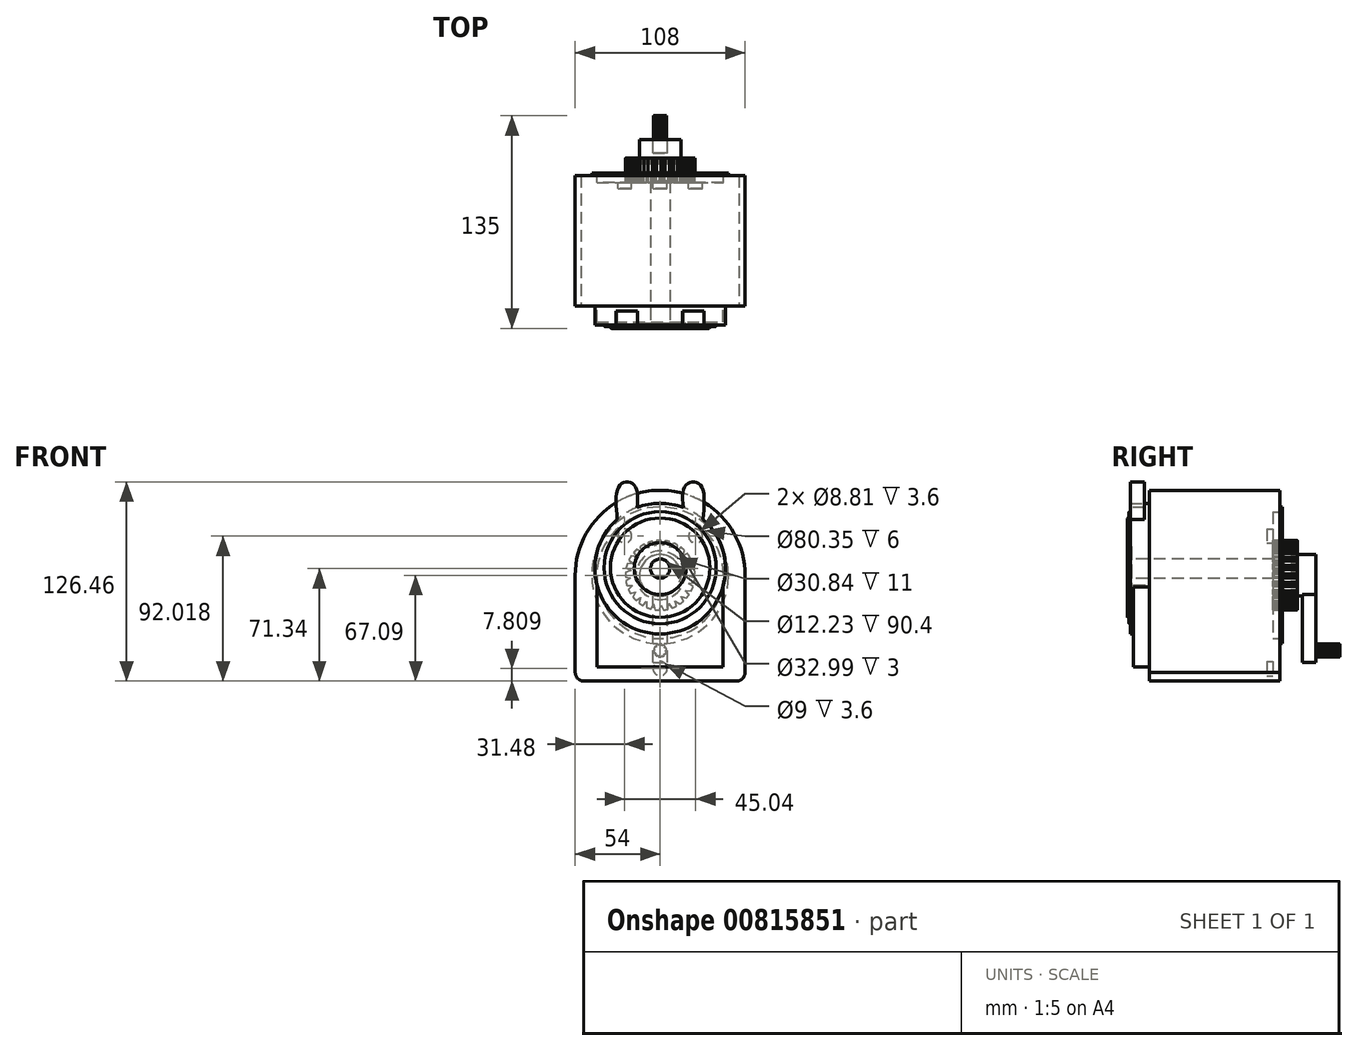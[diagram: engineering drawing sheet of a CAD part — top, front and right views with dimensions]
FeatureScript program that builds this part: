
annotation { "Feature Type Name" : "Feature", "Feature Type Description" : "" }
export const myFeature = defineFeature(function(context is Context, id is Id, definition is map)
    precondition{}
    {
        {
            var Q0;
            Q0=qCreatedBy(makeId("Front.planeOp"),FACE);
            var sketch = newSketch(context, id + "F0", { "sketchPlane" : qUnion([Q0])});
            skLineSegment(sketch, "E0.bottom", {"start": v(54, 61) * mm, "end": v(-54, 61) * mm});
            skLineSegment(sketch, "E0.top", {"start": v(54, -61) * mm, "end": v(-54, -61) * mm});
            skLineSegment(sketch, "E0.left", {"start": v(54, 61) * mm, "end": v(54, -61) * mm});
            skLineSegment(sketch, "E0.right", {"start": v(-54, 61) * mm, "end": v(-54, -61) * mm});
            skPoint(sketch, "E0.middle", {"position": v(0, 0) * mm});
            skSolve(sketch);
        }
        {
            var Q0;
            Q0=makeQuery(id+"F0.imprint","IMPRINT",FACE,{"disambiguationData":[TD([[makeQuery(id+"F0.imprint","IMPRINT",EDGE,{"derivedFrom":sQuery(id+"F0.wireOp",EDGE,"E0.bottom")}),1.0]])]});
            extrude(context, id + "F1", {"entities" : qUnion([Q0]), "depth" : 54 * mm, "offsetDistance" : 25 * mm});
        }
        {
            var Q0;
            Q0=makeQuery(id+"F1.opExtrude","CAP_FACE",FACE,{"disambiguationData":[OSD([sQuery(id+"F0.wireOp",EDGE,"E0.bottom"),sQuery(id+"F0.wireOp",EDGE,"E0.top"),sQuery(id+"F0.wireOp",EDGE,"E0.left"),sQuery(id+"F0.wireOp",EDGE,"E0.right")])],"isStart":true});
            extrude(context, id + "F2", {"entities" : qUnion([Q0]), "operationType" : NewBodyOperationType.ADD, "depth" : 29 * mm, "offsetDistance" : 25 * mm});
        }
        {
            var Q0;
            Q0=makeQuery(id+"F1.opExtrude","CAP_FACE",FACE,{"disambiguationData":[OSD([sQuery(id+"F0.wireOp",EDGE,"E0.bottom"),sQuery(id+"F0.wireOp",EDGE,"E0.top"),sQuery(id+"F0.wireOp",EDGE,"E0.left"),sQuery(id+"F0.wireOp",EDGE,"E0.right")])],"isStart":false});
            var sketch = newSketch(context, id + "F3", { "sketchPlane" : qUnion([Q0])});
            skCircle(sketch, "E1", {"center": v(0, 6.1) * mm, "radius": 54 * mm});
            skSolve(sketch);
        }
        {
            var Q0;
            {var subQ5=makeQuery(id+"F1.opExtrude","CAP_EDGE",EDGE,{"disambiguationData":[OSD([sQuery(id+"F0.wireOp",EDGE,"E0.bottom")])],"isStart":false});Q0=makeQuery(id+"F3.imprint","IMPRINT",FACE,{"disambiguationData":[TD([[makeQuery(id+"F3.imprint","IMPRINT",EDGE,{"derivedFrom":subQ5}),1.0]])]});}
            extrude(context, id + "F4", {"entities" : qUnion([Q0]), "operationType" : NewBodyOperationType.REMOVE, "oppositeDirection" : true, "depth" : 151.9 * mm, "offsetDistance" : 25 * mm});
        }
        {
            var Q0;
            Q0=makeQuery(id+"F1.opExtrude","CAP_FACE",FACE,{"disambiguationData":[OSD([sQuery(id+"F0.wireOp",EDGE,"E0.bottom"),sQuery(id+"F0.wireOp",EDGE,"E0.top"),sQuery(id+"F0.wireOp",EDGE,"E0.left"),sQuery(id+"F0.wireOp",EDGE,"E0.right")])],"isStart":false});
            var sketch = newSketch(context, id + "F5", { "sketchPlane" : qUnion([Q0])});
            skFitSpline(sketch, "E2", {"points": [v(54, -55.55) * mm, v(52.89, -58.83) * mm, v(50.2, -61) * mm], "startDerivative": vector(-1.44, -7.12) * mm, "endDerivative": vector(-6.17, -3.79) * mm});
            skFitSpline(sketch, "E3.MirrorCS", {"points": [v(-54, -55.55) * mm, v(-52.89, -58.83) * mm, v(-50.2, -61) * mm], "startDerivative": vector(1.44, -7.12) * mm, "endDerivative": vector(6.17, -3.79) * mm});
            skSolve(sketch);
        }
        {
            var Q0;
            {var subQ0=sQuery(id+"F5.wireOp",EDGE,"E3.MirrorCS");Q0=makeQuery(id+"F5.imprint","IMPRINT",FACE,{"disambiguationData":[TD([[makeQuery(id+"F5.imprint","IMPRINT",EDGE,{"derivedFrom":subQ0}),-1.0]])]});}
            extrude(context, id + "F6", {"entities" : qUnion([Q0]), "operationType" : NewBodyOperationType.REMOVE, "oppositeDirection" : true, "depth" : 499.5 * mm, "offsetDistance" : 25 * mm});
        }
        {
            var Q0;
            {var subQ0=sQuery(id+"F5.wireOp",EDGE,"E2");Q0=makeQuery(id+"F5.imprint","IMPRINT",FACE,{"disambiguationData":[TD([[makeQuery(id+"F5.imprint","IMPRINT",EDGE,{"derivedFrom":subQ0}),1.0]])]});}
            extrude(context, id + "F7", {"entities" : qUnion([Q0]), "operationType" : NewBodyOperationType.REMOVE, "oppositeDirection" : true, "depth" : 123.2 * mm, "offsetDistance" : 25 * mm});
        }
        {
            var Q0;
            Q0=makeQuery(id+"F1.opExtrude","CAP_FACE",FACE,{"disambiguationData":[OSD([sQuery(id+"F0.wireOp",EDGE,"E0.bottom"),sQuery(id+"F0.wireOp",EDGE,"E0.top"),sQuery(id+"F0.wireOp",EDGE,"E0.left"),sQuery(id+"F0.wireOp",EDGE,"E0.right")])],"isStart":false});
            var sketch = newSketch(context, id + "F8", { "sketchPlane" : qUnion([Q0])});
            skCircle(sketch, "E4", {"center": v(0, 10.34) * mm, "radius": 41.5 * mm});
            skLineSegment(sketch, "E5.bottom", {"start": v(-40.2, 0) * mm, "end": v(39.8, 0) * mm});
            skLineSegment(sketch, "E5.top", {"start": v(-40.2, -52) * mm, "end": v(39.8, -52) * mm});
            skLineSegment(sketch, "E5.left", {"start": v(-40.2, 0) * mm, "end": v(-40.2, -52) * mm});
            skLineSegment(sketch, "E5.right", {"start": v(39.8, 0) * mm, "end": v(39.8, -52) * mm});
            skSolve(sketch);
        }
        {
            var Q0;
            {var subQ0=sQuery(id+"F8.wireOp",EDGE,"E5.bottom");Q0=makeQuery(id+"F8.imprint","IMPRINT",FACE,{"disambiguationData":[TD([[makeQuery(id+"F8.imprint","IMPRINT",EDGE,{"derivedFrom":subQ0}),1.0]])]});}
            extrude(context, id + "F9", {"entities" : qUnion([Q0]), "operationType" : NewBodyOperationType.ADD, "depth" : 12 * mm, "offsetDistance" : 25 * mm});
        }
        {
            var Q0;
            {var subQ0=sQuery(id+"F8.wireOp",EDGE,"E5.bottom");Q0=makeQuery(id+"F8.imprint","IMPRINT",FACE,{"disambiguationData":[TD([[makeQuery(id+"F8.imprint","IMPRINT",EDGE,{"derivedFrom":subQ0}),-1.0]])]});}
            extrude(context, id + "F10", {"entities" : qUnion([Q0]), "operationType" : NewBodyOperationType.ADD, "depth" : 12 * mm, "offsetDistance" : 25 * mm});
        }
        {
            var Q0;
            {var subQ4=sQuery(id+"F8.wireOp",EDGE,"E5.top");Q0=makeQuery(id+"F8.imprint","IMPRINT",FACE,{"disambiguationData":[TD([[makeQuery(id+"F8.imprint","IMPRINT",EDGE,{"derivedFrom":subQ4}),1.0]])]});}
            extrude(context, id + "F11", {"entities" : qUnion([Q0]), "operationType" : NewBodyOperationType.ADD, "depth" : 10 * mm, "offsetDistance" : 25 * mm});
        }
        {
            var Q0;
            {var subQ0=sQuery(id+"F8.wireOp",EDGE,"E5.right");var subQ1=sQuery(id+"F8.wireOp",EDGE,"E5.bottom");var subQ2=sQuery(id+"F8.wireOp",EDGE,"E4");Q0=makeQuery(id+"F10.boolean.opBoolean","MERGE",FACE,{"derivedFrom":[makeQuery(id+"F9.opExtrude","CAP_FACE",FACE,{"disambiguationData":[OSD([subQ2,subQ1,subQ0])],"isStart":false}),makeQuery(id+"F10.opExtrude","CAP_FACE",FACE,{"disambiguationData":[OSD([subQ2,subQ1,subQ0])],"isStart":false})]});}
            var sketch = newSketch(context, id + "F12", { "sketchPlane" : qUnion([Q0])});
            skCircle(sketch, "E6", {"center": v(0, 10.34) * mm, "radius": 16.5 * mm});
            skCircle(sketch, "E7", {"center": v(0, 10.34) * mm, "radius": 6.12 * mm});
            skSolve(sketch);
        }
        {
            var Q0;
            Q0=makeQuery(id+"F12.imprint","IMPRINT",FACE,{"disambiguationData":[TD([[makeQuery(id+"F12.imprint","IMPRINT",EDGE,{"derivedFrom":sQuery(id+"F12.wireOp",EDGE,"E6")}),1.0]])]});
            extrude(context, id + "F13", {"entities" : qUnion([Q0]), "operationType" : NewBodyOperationType.REMOVE, "oppositeDirection" : true, "depth" : 1 * mm, "offsetDistance" : 25 * mm});
        }
        {
            var Q0;
            {var subQ0=sQuery(id+"F8.wireOp",EDGE,"E5.right");var subQ1=sQuery(id+"F8.wireOp",EDGE,"E5.bottom");var subQ2=sQuery(id+"F8.wireOp",EDGE,"E4");Q0=makeQuery(id+"F13.boolean.opBoolean","SPLIT",FACE,{"disambiguationData":[TD([makeQuery(id+"F13.opExtrude","SWEPT_FACE",FACE,{"disambiguationData":[OSD([sQuery(id+"F12.wireOp",EDGE,"E7")])]})])],"derivedFrom":makeQuery(id+"F10.boolean.opBoolean","MERGE",FACE,{"derivedFrom":[makeQuery(id+"F9.opExtrude","CAP_FACE",FACE,{"disambiguationData":[OSD([subQ2,subQ1,subQ0])],"isStart":false}),makeQuery(id+"F10.opExtrude","CAP_FACE",FACE,{"disambiguationData":[OSD([subQ2,subQ1,subQ0])],"isStart":false})]})});}
            extrude(context, id + "F14", {"entities" : qUnion([Q0]), "operationType" : NewBodyOperationType.REMOVE, "oppositeDirection" : true, "depth" : 91.4 * mm, "offsetDistance" : 25 * mm});
        }
        {
            var Q0;
            Q0=makeQuery(id+"F2.opExtrude","CAP_FACE",FACE,{"disambiguationData":[OSD([sQuery(id+"F0.wireOp",EDGE,"E0.bottom"),sQuery(id+"F0.wireOp",EDGE,"E0.top"),sQuery(id+"F0.wireOp",EDGE,"E0.left"),sQuery(id+"F0.wireOp",EDGE,"E0.right")])],"isStart":false});
            var sketch = newSketch(context, id + "F15", { "sketchPlane" : qUnion([Q0])});
            skCircle(sketch, "E8", {"center": v(0, 6.1) * mm, "radius": 22.12 * mm});
            skCircle(sketch, "E9", {"center": v(0, 6.1) * mm, "radius": 15.42 * mm});
            skCircle(sketch, "E10", {"center": v(0, 6.1) * mm, "radius": 13.17 * mm});
            skCircle(sketch, "E11", {"center": v(0, 6.1) * mm, "radius": 43.43 * mm});
            skCircle(sketch, "E12", {"center": v(0, 6.1) * mm, "radius": 40.17 * mm});
            skSolve(sketch);
        }
        {
            var Q0;
            Q0=makeQuery(id+"F15.imprint","IMPRINT",FACE,{"disambiguationData":[TD([[makeQuery(id+"F15.imprint","IMPRINT",EDGE,{"derivedFrom":sQuery(id+"F15.wireOp",EDGE,"E8")}),1.0]])]});
            extrude(context, id + "F16", {"entities" : qUnion([Q0]), "operationType" : NewBodyOperationType.ADD, "depth" : 11 * mm, "offsetDistance" : 25 * mm});
        }
        {
            var Q0;
            Q0=makeQuery(id+"F15.imprint","IMPRINT",FACE,{"disambiguationData":[TD([[makeQuery(id+"F15.imprint","IMPRINT",EDGE,{"derivedFrom":sQuery(id+"F15.wireOp",EDGE,"E10")}),1.0]])]});
            extrude(context, id + "F17", {"entities" : qUnion([Q0]), "operationType" : NewBodyOperationType.ADD, "depth" : 23 * mm, "offsetDistance" : 25 * mm});
        }
        {
            var Q0;
            Q0=makeQuery(id+"F17.opExtrude","CAP_FACE",FACE,{"disambiguationData":[OSD([sQuery(id+"F15.wireOp",EDGE,"E10")])],"isStart":false});
            var sketch = newSketch(context, id + "F18", { "sketchPlane" : qUnion([Q0])});
            skLineSegment(sketch, "E13.bottom", {"start": v(4.67, -49.15) * mm, "end": v(-4.67, -49.15) * mm});
            skLineSegment(sketch, "E13.top", {"start": v(4.67, 5.8) * mm, "end": v(-4.67, 5.8) * mm});
            skLineSegment(sketch, "E13.left", {"start": v(4.67, -49.15) * mm, "end": v(4.67, 5.8) * mm});
            skLineSegment(sketch, "E13.right", {"start": v(-4.67, -49.15) * mm, "end": v(-4.67, 5.8) * mm});
            skPoint(sketch, "E13.middle", {"position": v(0, -21.67) * mm});
            skSolve(sketch);
        }
        {
            var Q0;
            {var subQ0=sQuery(id+"F18.wireOp",EDGE,"E13.bottom");Q0=makeQuery(id+"F18.imprint","IMPRINT",FACE,{"disambiguationData":[TD([[makeQuery(id+"F18.imprint","IMPRINT",EDGE,{"derivedFrom":subQ0}),-1.0]])]});}
            var Q1;
            {var subQ0=sQuery(id+"F18.wireOp",EDGE,"E13.top");Q1=makeQuery(id+"F18.imprint","IMPRINT",FACE,{"disambiguationData":[TD([[makeQuery(id+"F18.imprint","IMPRINT",EDGE,{"derivedFrom":subQ0}),1.0]])]});}
            extrude(context, id + "F19", {"entities" : qUnion([Q0, Q1]), "operationType" : NewBodyOperationType.ADD, "oppositeDirection" : true, "depth" : 8.6 * mm, "offsetDistance" : 25 * mm});
        }
        {
            var Q0;
            Q0=makeQuery(id+"F19.boolean.opBoolean","MERGE",FACE,{"derivedFrom":[makeQuery(id+"F17.opExtrude","CAP_FACE",FACE,{"disambiguationData":[OSD([sQuery(id+"F15.wireOp",EDGE,"E10")])],"isStart":false}),makeQuery(id+"F19.opExtrude","CAP_FACE",FACE,{"disambiguationData":[OSD([sQuery(id+"F18.wireOp",EDGE,"E13.bottom"),sQuery(id+"F18.wireOp",EDGE,"E13.top"),sQuery(id+"F18.wireOp",EDGE,"E13.left"),sQuery(id+"F18.wireOp",EDGE,"E13.right")])],"isStart":true})]});
            var sketch = newSketch(context, id + "F20", { "sketchPlane" : qUnion([Q0])});
            skCircle(sketch, "E14", {"center": v(0, -41.66) * mm, "radius": 4.08 * mm});
            skSolve(sketch);
        }
        {
            var Q0;
            Q0=makeQuery(id+"F20.imprint","IMPRINT",FACE,{"disambiguationData":[TD([[makeQuery(id+"F20.imprint","IMPRINT",EDGE,{"derivedFrom":sQuery(id+"F20.wireOp",EDGE,"E14")}),1.0]])]});
            extrude(context, id + "F21", {"entities" : qUnion([Q0]), "operationType" : NewBodyOperationType.ADD, "depth" : 15 * mm, "offsetDistance" : 25 * mm});
        }
        {
            var Q0;
            {var subQ0=sQuery(id+"F8.wireOp",EDGE,"E4");var subQ1=sQuery(id+"F8.wireOp",EDGE,"E5.right");var subQ2=sQuery(id+"F8.wireOp",EDGE,"E5.bottom");Q0=makeQuery(id+"F13.boolean.opBoolean","SPLIT",FACE,{"disambiguationData":[TD([makeQuery(id+"F9.opExtrude","SWEPT_FACE",FACE,{"disambiguationData":[OSD([subQ0])]})])],"derivedFrom":makeQuery(id+"F10.boolean.opBoolean","MERGE",FACE,{"derivedFrom":[makeQuery(id+"F9.opExtrude","CAP_FACE",FACE,{"disambiguationData":[OSD([subQ0,subQ2,subQ1])],"isStart":false}),makeQuery(id+"F10.opExtrude","CAP_FACE",FACE,{"disambiguationData":[OSD([subQ0,subQ2,subQ1])],"isStart":false})]})});}
            var sketch = newSketch(context, id + "F22", { "sketchPlane" : qUnion([Q0])});
            skFitSpline(sketch, "E15", {"points": [v(15.46, 43.66) * mm, v(15.27, 61.68) * mm, v(20.61, 65.45) * mm, v(26.42, 62.27) * mm, v(27.26, 41.63) * mm], "startDerivative": vector(-9.71, 69.25) * mm, "endDerivative": vector(-6.88, -76) * mm});
            skFitSpline(sketch, "E16.MirrorCS", {"points": [v(-15.46, 43.66) * mm, v(-15.27, 61.68) * mm, v(-20.61, 65.45) * mm, v(-26.42, 62.27) * mm, v(-27.26, 41.63) * mm], "startDerivative": vector(9.71, 69.25) * mm, "endDerivative": vector(6.88, -76) * mm});
            skLineSegment(sketch, "E17", {"start": v(-27.26, 41.63) * mm, "end": v(-15.46, 43.66) * mm});
            skLineSegment(sketch, "E18", {"start": v(15.46, 43.66) * mm, "end": v(27.26, 41.63) * mm});
            skSolve(sketch);
        }
        {
            var Q0;
            Q0 = qSketchRegion(id + "F22", true);
            extrude(context, id + "F23", {"entities" : qUnion([Q0]), "operationType" : NewBodyOperationType.ADD, "oppositeDirection" : true, "depth" : 9 * mm, "offsetDistance" : 25 * mm});
        }
        {
            var Q0;
            Q0=makeQuery(id+"F15.imprint","IMPRINT",FACE,{"disambiguationData":[TD([[makeQuery(id+"F15.imprint","IMPRINT",EDGE,{"derivedFrom":sQuery(id+"F15.wireOp",EDGE,"E8")}),-1.0]])]});
            extrude(context, id + "F24", {"entities" : qUnion([Q0]), "operationType" : NewBodyOperationType.REMOVE, "oppositeDirection" : true, "depth" : 4.5 * mm, "offsetDistance" : 25 * mm});
        }
        {
            var Q0;
            Q0=makeQuery(id+"F15.imprint","IMPRINT",FACE,{"disambiguationData":[TD([[makeQuery(id+"F15.imprint","IMPRINT",EDGE,{"derivedFrom":sQuery(id+"F15.wireOp",EDGE,"E11")}),1.0]])]});
            extrude(context, id + "F25", {"entities" : qUnion([Q0]), "operationType" : NewBodyOperationType.ADD, "depth" : 1.5 * mm, "offsetDistance" : 25 * mm});
        }
        {
            var Q0;
            Q0=makeQuery(id+"F24.boolean.opBoolean","COPY",FACE,{"derivedFrom":makeQuery(id+"F24.opExtrude","CAP_FACE",FACE,{"disambiguationData":[OSD([sQuery(id+"F15.wireOp",EDGE,"E8"),sQuery(id+"F15.wireOp",EDGE,"E12")])],"isStart":false})});
            var sketch = newSketch(context, id + "F26", { "sketchPlane" : qUnion([Q0])});
            skCircle(sketch, "E19", {"center": v(-22.52, 31.02) * mm, "radius": 4.4 * mm});
            skCircle(sketch, "E20.MirrorC", {"center": v(22.52, 31.02) * mm, "radius": 4.4 * mm});
            skCircle(sketch, "E21", {"center": v(0, -53.2) * mm, "radius": 4.5 * mm});
            skSolve(sketch);
        }
        {
            var Q0;
            Q0 = qSketchRegion(id + "F26", true);
            extrude(context, id + "F27", {"entities" : qUnion([Q0]), "operationType" : NewBodyOperationType.REMOVE, "oppositeDirection" : true, "depth" : 3.6 * mm, "offsetDistance" : 25 * mm});
        }
        {
            var Q0;
            Q0=makeQuery(id+"F16.opExtrude","CAP_FACE",FACE,{"disambiguationData":[OSD([sQuery(id+"F15.wireOp",EDGE,"E8"),sQuery(id+"F15.wireOp",EDGE,"E9")])],"isStart":false});
            var sketch = newSketch(context, id + "F28", { "sketchPlane" : qUnion([Q0])});
            skLineSegment(sketch, "E22", {"start": v(-17.31, 19.87) * mm, "end": v(-14.1, 18.47) * mm});
            skLineSegment(sketch, "E23", {"start": v(-14.1, 18.47) * mm, "end": v(-15.52, 21.86) * mm});
            skLineSegment(sketch, "E24.1.0", {"start": v(-16.74, 14.57) * mm, "end": v(-18.96, 17.5) * mm});
            skLineSegment(sketch, "E24.1.1", {"start": v(-20.2, 15.13) * mm, "end": v(-16.74, 14.57) * mm});
            skLineSegment(sketch, "E24.2.0", {"start": v(-18.32, 10.14) * mm, "end": v(-21.2, 12.43) * mm});
            skLineSegment(sketch, "E24.2.1", {"start": v(-21.8, 9.82) * mm, "end": v(-18.32, 10.14) * mm});
            skLineSegment(sketch, "E24.3.0", {"start": v(-18.75, 5.46) * mm, "end": v(-22.1, 6.96) * mm});
            skLineSegment(sketch, "E24.3.1", {"start": v(-22.05, 4.28) * mm, "end": v(-18.75, 5.46) * mm});
            skLineSegment(sketch, "E24.4.0", {"start": v(-18, 0.81) * mm, "end": v(-21.63, 1.43) * mm});
            skLineSegment(sketch, "E24.4.1", {"start": v(-20.9, -1.15) * mm, "end": v(-18, 0.81) * mm});
            skLineSegment(sketch, "E24.5.0", {"start": v(-16.13, -3.5) * mm, "end": v(-19.8, -3.8) * mm});
            skLineSegment(sketch, "E24.5.1", {"start": v(-18.45, -6.12) * mm, "end": v(-16.13, -3.5) * mm});
            skLineSegment(sketch, "E24.6.0", {"start": v(-13.24, -7.21) * mm, "end": v(-16.7, -8.41) * mm});
            skLineSegment(sketch, "E24.6.1", {"start": v(-14.84, -10.32) * mm, "end": v(-13.24, -7.21) * mm});
            skLineSegment(sketch, "E24.7.0", {"start": v(-9.51, -10.08) * mm, "end": v(-12.58, -12.11) * mm});
            skLineSegment(sketch, "E24.7.1", {"start": v(-10.29, -13.5) * mm, "end": v(-9.51, -10.08) * mm});
            skLineSegment(sketch, "E24.8.0", {"start": v(-5.2, -11.94) * mm, "end": v(-7.65, -14.67) * mm});
            skLineSegment(sketch, "E24.8.1", {"start": v(-5.1, -15.44) * mm, "end": v(-5.2, -11.94) * mm});
            skLineSegment(sketch, "E24.9.0", {"start": v(-0.54, -12.67) * mm, "end": v(-2.25, -15.92) * mm});
            skLineSegment(sketch, "E24.9.1", {"start": v(0.42, -16.03) * mm, "end": v(-0.54, -12.67) * mm});
            skLineSegment(sketch, "E24.10.0", {"start": v(4.14, -12.21) * mm, "end": v(3.3, -15.79) * mm});
            skLineSegment(sketch, "E24.10.1", {"start": v(5.9, -15.23) * mm, "end": v(4.14, -12.21) * mm});
            skLineSegment(sketch, "E24.11.0", {"start": v(8.56, -10.6) * mm, "end": v(8.63, -14.28) * mm});
            skLineSegment(sketch, "E24.11.1", {"start": v(11.03, -13.1) * mm, "end": v(8.56, -10.6) * mm});
            skLineSegment(sketch, "E24.12.0", {"start": v(12.44, -7.96) * mm, "end": v(13.43, -11.5) * mm});
            skLineSegment(sketch, "E24.12.1", {"start": v(15.45, -9.75) * mm, "end": v(12.44, -7.96) * mm});
            skLineSegment(sketch, "E24.13.0", {"start": v(15.55, -4.42) * mm, "end": v(17.38, -7.6) * mm});
            skLineSegment(sketch, "E24.13.1", {"start": v(18.9, -5.4) * mm, "end": v(15.55, -4.42) * mm});
            skLineSegment(sketch, "E24.14.0", {"start": v(17.67, -0.22) * mm, "end": v(20.24, -2.85) * mm});
            skLineSegment(sketch, "E24.14.1", {"start": v(21.17, -0.34) * mm, "end": v(17.67, -0.22) * mm});
            skLineSegment(sketch, "E24.15.0", {"start": v(18.69, 4.37) * mm, "end": v(21.83, 2.46) * mm});
            skLineSegment(sketch, "E24.15.1", {"start": v(22.1, 5.12) * mm, "end": v(18.69, 4.37) * mm});
            skLineSegment(sketch, "E24.16.0", {"start": v(18.53, 9.07) * mm, "end": v(22.04, 8) * mm});
            skLineSegment(sketch, "E24.16.1", {"start": v(21.65, 10.65) * mm, "end": v(18.53, 9.07) * mm});
            skLineSegment(sketch, "E24.17.0", {"start": v(17.2, 13.58) * mm, "end": v(20.87, 13.42) * mm});
            skLineSegment(sketch, "E24.17.1", {"start": v(19.84, 15.9) * mm, "end": v(17.2, 13.58) * mm});
            skLineSegment(sketch, "E24.18.0", {"start": v(14.8, 17.63) * mm, "end": v(18.4, 18.38) * mm});
            skLineSegment(sketch, "E24.18.1", {"start": v(16.78, 20.52) * mm, "end": v(14.8, 17.63) * mm});
            skLineSegment(sketch, "E24.19.0", {"start": v(11.47, 20.94) * mm, "end": v(14.76, 22.57) * mm});
            skLineSegment(sketch, "E24.19.1", {"start": v(12.66, 24.23) * mm, "end": v(11.47, 20.94) * mm});
            skLineSegment(sketch, "E24.20.0", {"start": v(7.41, 23.33) * mm, "end": v(10.2, 25.73) * mm});
            skLineSegment(sketch, "E24.20.1", {"start": v(7.75, 26.81) * mm, "end": v(7.41, 23.33) * mm});
            skLineSegment(sketch, "E24.21.0", {"start": v(2.9, 24.63) * mm, "end": v(5, 27.64) * mm});
            skLineSegment(sketch, "E24.21.1", {"start": v(2.35, 28.09) * mm, "end": v(2.9, 24.63) * mm});
            skLineSegment(sketch, "E24.22.0", {"start": v(-1.81, 24.77) * mm, "end": v(-0.52, 28.2) * mm});
            skLineSegment(sketch, "E24.22.1", {"start": v(-3.2, 27.98) * mm, "end": v(-1.81, 24.77) * mm});
            skLineSegment(sketch, "E24.23.0", {"start": v(-6.4, 23.73) * mm, "end": v(-6, 27.38) * mm});
            skLineSegment(sketch, "E24.23.1", {"start": v(-8.54, 26.5) * mm, "end": v(-6.4, 23.73) * mm});
            skLineSegment(sketch, "E24.24.0", {"start": v(-10.58, 21.58) * mm, "end": v(-11.12, 25.22) * mm});
            skLineSegment(sketch, "E24.24.1", {"start": v(-13.34, 23.74) * mm, "end": v(-10.58, 21.58) * mm});
            skPoint(sketch, "E24.center", {"position": v(0, 6.1) * mm});
            skSolve(sketch);
        }
        {
            var Q0;
            {var subQ0=sQuery(id+"F28.wireOp",EDGE,"E22");Q0=makeQuery(id+"F28.imprint","IMPRINT",FACE,{"disambiguationData":[TD([[makeQuery(id+"F28.imprint","IMPRINT",EDGE,{"derivedFrom":subQ0}),1.0]])]});}
            var Q1;
            {var subQ0=sQuery(id+"F28.wireOp",EDGE,"E24.1.0");Q1=makeQuery(id+"F28.imprint","IMPRINT",FACE,{"disambiguationData":[TD([[makeQuery(id+"F28.imprint","IMPRINT",EDGE,{"derivedFrom":subQ0}),1.0]])]});}
            var Q2;
            {var subQ0=sQuery(id+"F28.wireOp",EDGE,"E24.2.0");Q2=makeQuery(id+"F28.imprint","IMPRINT",FACE,{"disambiguationData":[TD([[makeQuery(id+"F28.imprint","IMPRINT",EDGE,{"derivedFrom":subQ0}),1.0]])]});}
            var Q3;
            {var subQ0=sQuery(id+"F28.wireOp",EDGE,"E24.3.0");Q3=makeQuery(id+"F28.imprint","IMPRINT",FACE,{"disambiguationData":[TD([[makeQuery(id+"F28.imprint","IMPRINT",EDGE,{"derivedFrom":subQ0}),1.0]])]});}
            var Q4;
            {var subQ0=sQuery(id+"F28.wireOp",EDGE,"E24.24.0");Q4=makeQuery(id+"F28.imprint","IMPRINT",FACE,{"disambiguationData":[TD([[makeQuery(id+"F28.imprint","IMPRINT",EDGE,{"derivedFrom":subQ0}),1.0]])]});}
            var Q5;
            {var subQ0=sQuery(id+"F28.wireOp",EDGE,"E24.23.0");Q5=makeQuery(id+"F28.imprint","IMPRINT",FACE,{"disambiguationData":[TD([[makeQuery(id+"F28.imprint","IMPRINT",EDGE,{"derivedFrom":subQ0}),1.0]])]});}
            var Q6;
            {var subQ0=sQuery(id+"F28.wireOp",EDGE,"E24.22.0");Q6=makeQuery(id+"F28.imprint","IMPRINT",FACE,{"disambiguationData":[TD([[makeQuery(id+"F28.imprint","IMPRINT",EDGE,{"derivedFrom":subQ0}),1.0]])]});}
            var Q7;
            {var subQ0=sQuery(id+"F28.wireOp",EDGE,"E24.21.0");Q7=makeQuery(id+"F28.imprint","IMPRINT",FACE,{"disambiguationData":[TD([[makeQuery(id+"F28.imprint","IMPRINT",EDGE,{"derivedFrom":subQ0}),1.0]])]});}
            var Q8;
            {var subQ0=sQuery(id+"F28.wireOp",EDGE,"E24.20.0");Q8=makeQuery(id+"F28.imprint","IMPRINT",FACE,{"disambiguationData":[TD([[makeQuery(id+"F28.imprint","IMPRINT",EDGE,{"derivedFrom":subQ0}),1.0]])]});}
            var Q9;
            {var subQ0=sQuery(id+"F28.wireOp",EDGE,"E24.19.0");Q9=makeQuery(id+"F28.imprint","IMPRINT",FACE,{"disambiguationData":[TD([[makeQuery(id+"F28.imprint","IMPRINT",EDGE,{"derivedFrom":subQ0}),1.0]])]});}
            var Q10;
            {var subQ0=sQuery(id+"F28.wireOp",EDGE,"E24.18.0");Q10=makeQuery(id+"F28.imprint","IMPRINT",FACE,{"disambiguationData":[TD([[makeQuery(id+"F28.imprint","IMPRINT",EDGE,{"derivedFrom":subQ0}),1.0]])]});}
            var Q11;
            {var subQ0=sQuery(id+"F28.wireOp",EDGE,"E24.17.0");Q11=makeQuery(id+"F28.imprint","IMPRINT",FACE,{"disambiguationData":[TD([[makeQuery(id+"F28.imprint","IMPRINT",EDGE,{"derivedFrom":subQ0}),1.0]])]});}
            var Q12;
            {var subQ0=sQuery(id+"F28.wireOp",EDGE,"E24.16.0");Q12=makeQuery(id+"F28.imprint","IMPRINT",FACE,{"disambiguationData":[TD([[makeQuery(id+"F28.imprint","IMPRINT",EDGE,{"derivedFrom":subQ0}),1.0]])]});}
            var Q13;
            {var subQ0=sQuery(id+"F28.wireOp",EDGE,"E24.15.0");Q13=makeQuery(id+"F28.imprint","IMPRINT",FACE,{"disambiguationData":[TD([[makeQuery(id+"F28.imprint","IMPRINT",EDGE,{"derivedFrom":subQ0}),1.0]])]});}
            var Q14;
            {var subQ0=sQuery(id+"F28.wireOp",EDGE,"E24.14.0");Q14=makeQuery(id+"F28.imprint","IMPRINT",FACE,{"disambiguationData":[TD([[makeQuery(id+"F28.imprint","IMPRINT",EDGE,{"derivedFrom":subQ0}),1.0]])]});}
            var Q15;
            {var subQ0=sQuery(id+"F28.wireOp",EDGE,"E24.11.0");Q15=makeQuery(id+"F28.imprint","IMPRINT",FACE,{"disambiguationData":[TD([[makeQuery(id+"F28.imprint","IMPRINT",EDGE,{"derivedFrom":subQ0}),1.0]])]});}
            var Q16;
            {var subQ0=sQuery(id+"F28.wireOp",EDGE,"E24.12.0");Q16=makeQuery(id+"F28.imprint","IMPRINT",FACE,{"disambiguationData":[TD([[makeQuery(id+"F28.imprint","IMPRINT",EDGE,{"derivedFrom":subQ0}),1.0]])]});}
            var Q17;
            {var subQ0=sQuery(id+"F28.wireOp",EDGE,"E24.13.0");Q17=makeQuery(id+"F28.imprint","IMPRINT",FACE,{"disambiguationData":[TD([[makeQuery(id+"F28.imprint","IMPRINT",EDGE,{"derivedFrom":subQ0}),1.0]])]});}
            var Q18;
            {var subQ0=sQuery(id+"F28.wireOp",EDGE,"E24.10.0");Q18=makeQuery(id+"F28.imprint","IMPRINT",FACE,{"disambiguationData":[TD([[makeQuery(id+"F28.imprint","IMPRINT",EDGE,{"derivedFrom":subQ0}),1.0]])]});}
            var Q19;
            {var subQ0=sQuery(id+"F28.wireOp",EDGE,"E24.9.0");Q19=makeQuery(id+"F28.imprint","IMPRINT",FACE,{"disambiguationData":[TD([[makeQuery(id+"F28.imprint","IMPRINT",EDGE,{"derivedFrom":subQ0}),1.0]])]});}
            var Q20;
            {var subQ0=sQuery(id+"F28.wireOp",EDGE,"E24.8.0");Q20=makeQuery(id+"F28.imprint","IMPRINT",FACE,{"disambiguationData":[TD([[makeQuery(id+"F28.imprint","IMPRINT",EDGE,{"derivedFrom":subQ0}),1.0]])]});}
            var Q21;
            {var subQ0=sQuery(id+"F28.wireOp",EDGE,"E24.7.0");Q21=makeQuery(id+"F28.imprint","IMPRINT",FACE,{"disambiguationData":[TD([[makeQuery(id+"F28.imprint","IMPRINT",EDGE,{"derivedFrom":subQ0}),1.0]])]});}
            var Q22;
            {var subQ0=sQuery(id+"F28.wireOp",EDGE,"E24.5.0");Q22=makeQuery(id+"F28.imprint","IMPRINT",FACE,{"disambiguationData":[TD([[makeQuery(id+"F28.imprint","IMPRINT",EDGE,{"derivedFrom":subQ0}),1.0]])]});}
            var Q23;
            {var subQ0=sQuery(id+"F28.wireOp",EDGE,"E24.4.0");Q23=makeQuery(id+"F28.imprint","IMPRINT",FACE,{"disambiguationData":[TD([[makeQuery(id+"F28.imprint","IMPRINT",EDGE,{"derivedFrom":subQ0}),1.0]])]});}
            var Q24;
            {var subQ0=sQuery(id+"F28.wireOp",EDGE,"E24.6.0");Q24=makeQuery(id+"F28.imprint","IMPRINT",FACE,{"disambiguationData":[TD([[makeQuery(id+"F28.imprint","IMPRINT",EDGE,{"derivedFrom":subQ0}),1.0]])]});}
            extrude(context, id + "F29", {"entities" : qUnion([Q0, Q1, Q2, Q3, Q4, Q5, Q6, Q7, Q8, Q9, Q10, Q11, Q12, Q13, Q14, Q15, Q16, Q17, Q18, Q19, Q20, Q21, Q22, Q23, Q24]), "operationType" : NewBodyOperationType.REMOVE, "oppositeDirection" : true, "depth" : 15.5 * mm, "offsetDistance" : 25 * mm});
        }
        {
            var Q0;
            Q0=makeQuery(id+"F12.imprint","IMPRINT",FACE,{"disambiguationData":[TD([[makeQuery(id+"F12.imprint","IMPRINT",EDGE,{"derivedFrom":sQuery(id+"F12.wireOp",EDGE,"E6")}),-1.0]])]});
            var sketch = newSketch(context, id + "F30", { "sketchPlane" : qUnion([Q0])});
            skCircle(sketch, "E25", {"center": v(0, 10.9) * mm, "radius": 35.58 * mm});
            skCircle(sketch, "E26", {"center": v(0, 10.9) * mm, "radius": 31.59 * mm});
            skSolve(sketch);
        }
        {
            var Q0;
            Q0=makeQuery(id+"F30.imprint","IMPRINT",FACE,{"disambiguationData":[TD([[makeQuery(id+"F30.imprint","IMPRINT",EDGE,{"derivedFrom":sQuery(id+"F30.wireOp",EDGE,"E25")}),1.0]])]});
            extrude(context, id + "F31", {"entities" : qUnion([Q0]), "operationType" : NewBodyOperationType.ADD, "depth" : 1 * mm, "offsetDistance" : 25 * mm});
        }
        {
            var Q0;
            {var subQ0=makeQuery(id+"F13.opExtrude","SWEPT_FACE",FACE,{"disambiguationData":[OSD([sQuery(id+"F12.wireOp",EDGE,"E6")])]});var subQ1=sQuery(id+"F8.wireOp",EDGE,"E4");var subQ2=sQuery(id+"F8.wireOp",EDGE,"E5.right");var subQ3=sQuery(id+"F8.wireOp",EDGE,"E5.bottom");Q0=makeQuery(id+"F31.boolean.opBoolean","SPLIT",FACE,{"disambiguationData":[TD([makeQuery(id+"F13.boolean.opBoolean","COPY",FACE,{"derivedFrom":subQ0})])],"derivedFrom":makeQuery(id+"F23.boolean.opBoolean","MERGE",FACE,{"derivedFrom":[makeQuery(id+"F13.boolean.opBoolean","SPLIT",FACE,{"disambiguationData":[TD([makeQuery(id+"F9.opExtrude","SWEPT_FACE",FACE,{"disambiguationData":[OSD([subQ1])]})])],"derivedFrom":makeQuery(id+"F10.boolean.opBoolean","MERGE",FACE,{"derivedFrom":[makeQuery(id+"F9.opExtrude","CAP_FACE",FACE,{"disambiguationData":[OSD([subQ1,subQ3,subQ2])],"isStart":false}),makeQuery(id+"F10.opExtrude","CAP_FACE",FACE,{"disambiguationData":[OSD([subQ1,subQ3,subQ2])],"isStart":false})]})}),makeQuery(id+"F23.opExtrude","CAP_FACE",FACE,{"disambiguationData":[OSD([sQuery(id+"F22.wireOp",EDGE,"E15"),sQuery(id+"F22.wireOp",EDGE,"E18")])],"isStart":true}),makeQuery(id+"F23.opExtrude","CAP_FACE",FACE,{"disambiguationData":[OSD([sQuery(id+"F22.wireOp",EDGE,"E16.MirrorCS"),sQuery(id+"F22.wireOp",EDGE,"E17")])],"isStart":true})]})});}
            extrude(context, id + "F32", {"entities" : qUnion([Q0]), "operationType" : NewBodyOperationType.ADD, "depth" : 2 * mm, "offsetDistance" : 25 * mm});
        }
        {
            var Q0;
            Q0=makeQuery(id+"F31.opExtrude","CAP_EDGE",EDGE,{"disambiguationData":[OSD([sQuery(id+"F30.wireOp",EDGE,"E25")])],"isStart":false});
            fillet(context, id + "F33", {"entities" : qUnion([Q0]), "radius" : 0.7 * mm, "tangentPropagation" : true, "allowEdgeOverflow" : false});
        }
        {
            var Q0;
            Q0=makeQuery(id+"F32.opExtrude","CAP_EDGE",EDGE,{"disambiguationData":[OSD([sQuery(id+"F30.wireOp",EDGE,"E26")])],"isStart":false});
            fillet(context, id + "F34", {"entities" : qUnion([Q0]), "radius" : 0.7 * mm, "tangentPropagation" : true, "allowEdgeOverflow" : false});
        }
        {
            var Q0;
            Q0=makeQuery(id+"F21.opExtrude","CAP_FACE",FACE,{"disambiguationData":[OSD([sQuery(id+"F20.wireOp",EDGE,"E14")])],"isStart":false});
            var sketch = newSketch(context, id + "F35", { "sketchPlane" : qUnion([Q0])});
            skLineSegment(sketch, "E27", {"start": v(-3.73, -40) * mm, "end": v(-2.73, -40) * mm});
            skLineSegment(sketch, "E28", {"start": v(-2.73, -40) * mm, "end": v(-3.19, -39.1) * mm});
            skLineSegment(sketch, "E29.1.0", {"start": v(-4, -42.5) * mm, "end": v(-3.18, -41.92) * mm});
            skLineSegment(sketch, "E29.1.1", {"start": v(-3.18, -41.92) * mm, "end": v(-4.08, -41.47) * mm});
            skLineSegment(sketch, "E29.2.0", {"start": v(-2.73, -44.7) * mm, "end": v(-2.42, -43.74) * mm});
            skLineSegment(sketch, "E29.2.1", {"start": v(-2.42, -43.74) * mm, "end": v(-3.41, -43.9) * mm});
            skLineSegment(sketch, "E29.3.0", {"start": v(-0.43, -45.72) * mm, "end": v(-0.74, -44.77) * mm});
            skLineSegment(sketch, "E29.3.1", {"start": v(-0.74, -44.77) * mm, "end": v(-1.44, -45.48) * mm});
            skLineSegment(sketch, "E29.4.0", {"start": v(2.04, -45.2) * mm, "end": v(1.23, -44.6) * mm});
            skLineSegment(sketch, "E29.4.1", {"start": v(1.23, -44.6) * mm, "end": v(1.08, -45.6) * mm});
            skLineSegment(sketch, "E29.5.0", {"start": v(3.73, -43.32) * mm, "end": v(2.73, -43.32) * mm});
            skLineSegment(sketch, "E29.5.1", {"start": v(2.73, -43.32) * mm, "end": v(3.19, -44.2) * mm});
            skLineSegment(sketch, "E29.6.0", {"start": v(4, -40.81) * mm, "end": v(3.18, -41.4) * mm});
            skLineSegment(sketch, "E29.6.1", {"start": v(3.18, -41.4) * mm, "end": v(4.08, -41.85) * mm});
            skLineSegment(sketch, "E29.7.0", {"start": v(2.73, -38.62) * mm, "end": v(2.42, -39.58) * mm});
            skLineSegment(sketch, "E29.7.1", {"start": v(2.42, -39.58) * mm, "end": v(3.41, -39.41) * mm});
            skLineSegment(sketch, "E29.8.0", {"start": v(0.43, -37.6) * mm, "end": v(0.74, -38.55) * mm});
            skLineSegment(sketch, "E29.8.1", {"start": v(0.74, -38.55) * mm, "end": v(1.44, -37.84) * mm});
            skLineSegment(sketch, "E29.9.0", {"start": v(-2.04, -38.12) * mm, "end": v(-1.23, -38.7) * mm});
            skLineSegment(sketch, "E29.9.1", {"start": v(-1.23, -38.7) * mm, "end": v(-1.08, -37.72) * mm});
            skPoint(sketch, "E29.center", {"position": v(0, -41.66) * mm});
            skSolve(sketch);
        }
        {
            var Q0;
            {var subQ0=sQuery(id+"F35.wireOp",EDGE,"E29.7.0");Q0=makeQuery(id+"F35.imprint","IMPRINT",FACE,{"disambiguationData":[TD([[makeQuery(id+"F35.imprint","IMPRINT",EDGE,{"derivedFrom":subQ0}),1.0]])]});}
            var Q1;
            {var subQ0=sQuery(id+"F35.wireOp",EDGE,"E29.8.0");Q1=makeQuery(id+"F35.imprint","IMPRINT",FACE,{"disambiguationData":[TD([[makeQuery(id+"F35.imprint","IMPRINT",EDGE,{"derivedFrom":subQ0}),1.0]])]});}
            var Q2;
            {var subQ0=sQuery(id+"F35.wireOp",EDGE,"E29.9.0");Q2=makeQuery(id+"F35.imprint","IMPRINT",FACE,{"disambiguationData":[TD([[makeQuery(id+"F35.imprint","IMPRINT",EDGE,{"derivedFrom":subQ0}),1.0]])]});}
            var Q3;
            {var subQ0=sQuery(id+"F35.wireOp",EDGE,"E27");Q3=makeQuery(id+"F35.imprint","IMPRINT",FACE,{"disambiguationData":[TD([[makeQuery(id+"F35.imprint","IMPRINT",EDGE,{"derivedFrom":subQ0}),1.0]])]});}
            var Q4;
            {var subQ0=sQuery(id+"F35.wireOp",EDGE,"E29.1.0");Q4=makeQuery(id+"F35.imprint","IMPRINT",FACE,{"disambiguationData":[TD([[makeQuery(id+"F35.imprint","IMPRINT",EDGE,{"derivedFrom":subQ0}),1.0]])]});}
            var Q5;
            {var subQ0=sQuery(id+"F35.wireOp",EDGE,"E29.6.0");Q5=makeQuery(id+"F35.imprint","IMPRINT",FACE,{"disambiguationData":[TD([[makeQuery(id+"F35.imprint","IMPRINT",EDGE,{"derivedFrom":subQ0}),1.0]])]});}
            var Q6;
            {var subQ0=sQuery(id+"F35.wireOp",EDGE,"E29.5.0");Q6=makeQuery(id+"F35.imprint","IMPRINT",FACE,{"disambiguationData":[TD([[makeQuery(id+"F35.imprint","IMPRINT",EDGE,{"derivedFrom":subQ0}),1.0]])]});}
            var Q7;
            {var subQ0=sQuery(id+"F35.wireOp",EDGE,"E29.4.0");Q7=makeQuery(id+"F35.imprint","IMPRINT",FACE,{"disambiguationData":[TD([[makeQuery(id+"F35.imprint","IMPRINT",EDGE,{"derivedFrom":subQ0}),1.0]])]});}
            var Q8;
            {var subQ0=sQuery(id+"F35.wireOp",EDGE,"E29.3.0");Q8=makeQuery(id+"F35.imprint","IMPRINT",FACE,{"disambiguationData":[TD([[makeQuery(id+"F35.imprint","IMPRINT",EDGE,{"derivedFrom":subQ0}),1.0]])]});}
            var Q9;
            {var subQ0=sQuery(id+"F35.wireOp",EDGE,"E29.2.0");Q9=makeQuery(id+"F35.imprint","IMPRINT",FACE,{"disambiguationData":[TD([[makeQuery(id+"F35.imprint","IMPRINT",EDGE,{"derivedFrom":subQ0}),1.0]])]});}
            var Q10;
            Q10=makeQuery(id+"F19.boolean.opBoolean","MERGE",FACE,{"derivedFrom":[makeQuery(id+"F17.opExtrude","CAP_FACE",FACE,{"disambiguationData":[OSD([sQuery(id+"F15.wireOp",EDGE,"E10")])],"isStart":false}),makeQuery(id+"F19.opExtrude","CAP_FACE",FACE,{"disambiguationData":[OSD([sQuery(id+"F18.wireOp",EDGE,"E13.bottom"),sQuery(id+"F18.wireOp",EDGE,"E13.top"),sQuery(id+"F18.wireOp",EDGE,"E13.left"),sQuery(id+"F18.wireOp",EDGE,"E13.right")])],"isStart":true})]});
            extrude(context, id + "F36", {"entities" : qUnion([Q0, Q1, Q2, Q3, Q4, Q5, Q6, Q7, Q8, Q9]), "operationType" : NewBodyOperationType.REMOVE, "endBound" : BoundingType.UP_TO_SURFACE, "oppositeDirection" : true, "depth" : 15.5 * mm, "endBoundEntityFace" : qUnion([Q10]), "offsetDistance" : 25 * mm});
        }
    });
